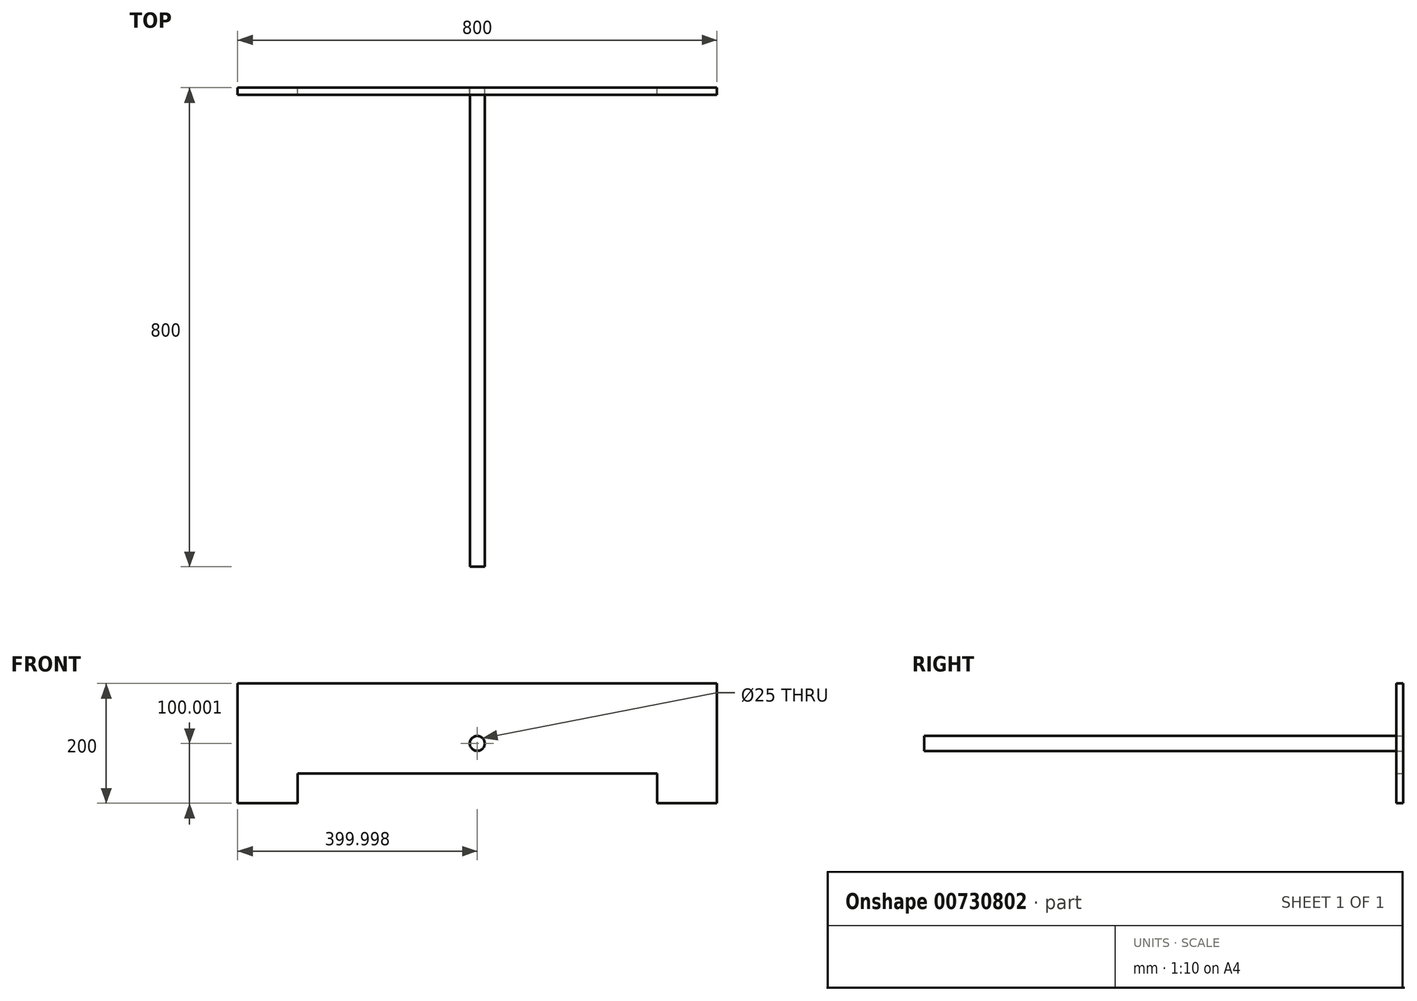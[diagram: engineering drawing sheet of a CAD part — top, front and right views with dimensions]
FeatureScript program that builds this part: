
annotation { "Feature Type Name" : "Feature", "Feature Type Description" : "" }
export const myFeature = defineFeature(function(context is Context, id is Id, definition is map)
    precondition{}
    {
        {
            var Q0;
            Q0=qCreatedBy(makeId("Front.planeOp"),FACE);
            var sketch = newSketch(context, id + "F0", { "sketchPlane" : qUnion([Q0])});
            skLineSegment(sketch, "E0.bottom", {"start": v(-451.4, 21.68) * mm, "end": v(348.6, 21.68) * mm});
            skLineSegment(sketch, "E0.top", {"start": v(-451.4, -178.32) * mm, "end": v(-351.4, -178.32) * mm});
            skLineSegment(sketch, "E0.left", {"start": v(-451.4, 21.68) * mm, "end": v(-451.4, -178.32) * mm});
            skLineSegment(sketch, "E0.right", {"start": v(348.6, 21.68) * mm, "end": v(348.6, -178.32) * mm});
            skCircle(sketch, "E1", {"center": v(-51.4, -78.32) * mm, "radius": 12.5 * mm});
            skPoint(sketch, "E1.centerSnap1", {"position": v(-451.4, -78.32) * mm});
            skLineSegment(sketch, "E2", {"start": v(-351.4, -128.32) * mm, "end": v(-351.4, -178.32) * mm});
            skLineSegment(sketch, "E3", {"start": v(248.6, -128.32) * mm, "end": v(248.6, -178.32) * mm});
            skLineSegment(sketch, "E4", {"start": v(-351.4, -128.32) * mm, "end": v(248.6, -128.32) * mm});
            skLineSegment(sketch, "E5", {"start": v(248.6, -178.32) * mm, "end": v(348.6, -178.32) * mm});
            skSolve(sketch);
        }
        {
            var Q0;
            Q0=qCreatedBy(makeId("Front.planeOp"),FACE);
            var sketch = newSketch(context, id + "F1", { "sketchPlane" : qUnion([Q0])});
            skCircle(sketch, "E6", {"center": v(-51.34, -78.32) * mm, "radius": 12.5 * mm});
            skSolve(sketch);
        }
        {
            var Q0;
            Q0 = qSketchRegion(id + "F0", true);
            extrude(context, id + "F2", {"entities" : qUnion([Q0]), "depth" : 12 * mm, "offsetDistance" : 25 * mm});
        }
        {
            var Q0;
            Q0 = qSketchRegion(id + "F1", true);
            extrude(context, id + "F3", {"entities" : qUnion([Q0]), "depth" : 800 * mm, "offsetDistance" : 25 * mm});
        }
    });
